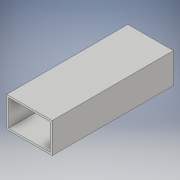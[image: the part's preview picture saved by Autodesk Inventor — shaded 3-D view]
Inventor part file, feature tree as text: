
AUTODESK INVENTOR PART (.ipt)
format: ipt  version: 2019 (Build 230136000, 136)  size: 94,208 bytes
history: native  units: in
note: dims shown in document units (in); Inventor stores cm internally (conversion verified against a paired STEP export)
features: extrude x1, sketch x1
ambient origin geometry x8: Origin, YZ Plane, XZ Plane, XY Plane, X Axis, Y Axis, Z Axis, Center Point
bodies: Solid1 (feature_tree)
feature tree (2):
  extrude  "Extrusion1"  Depth=2.0in
  sketch  "Sketch1"  dims[d0=3.0in d1=2.0in d2=0.125in d3=8.0in d4=0.0in]
